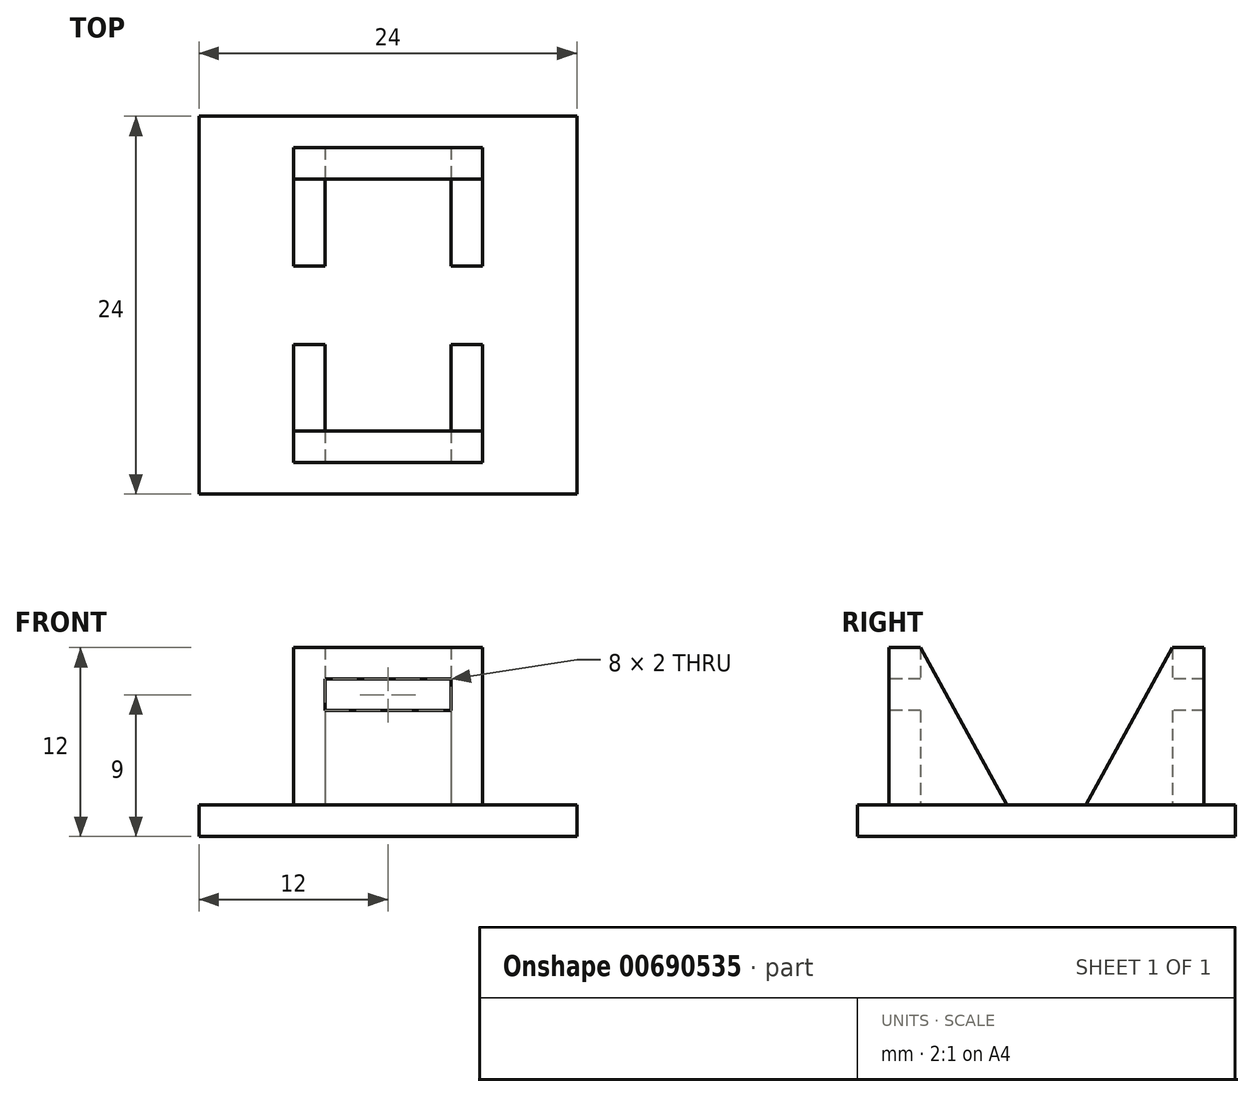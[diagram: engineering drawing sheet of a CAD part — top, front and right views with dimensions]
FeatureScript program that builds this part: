
annotation { "Feature Type Name" : "Feature", "Feature Type Description" : "" }
export const myFeature = defineFeature(function(context is Context, id is Id, definition is map)
    precondition{}
    {
        {
            var Q0;
            Q0=qCreatedBy(makeId("Top.planeOp"),FACE);
            var sketch = newSketch(context, id + "F0", { "sketchPlane" : qUnion([Q0])});
            skLineSegment(sketch, "E0.bottom", {"start": v(12, 12) * mm, "end": v(-12, 12) * mm});
            skLineSegment(sketch, "E0.top", {"start": v(12, -12) * mm, "end": v(-12, -12) * mm});
            skLineSegment(sketch, "E0.left", {"start": v(12, 12) * mm, "end": v(12, -12) * mm});
            skLineSegment(sketch, "E0.right", {"start": v(-12, 12) * mm, "end": v(-12, -12) * mm});
            skPoint(sketch, "E0.middle", {"position": v(0, 0) * mm});
            skLineSegment(sketch, "E1", {"start": v(0, 0) * mm, "end": v(-12, 0) * mm, "construction": true});
            skLineSegment(sketch, "E2", {"start": v(-6, 0) * mm, "end": v(-6, 2.5) * mm, "construction": true});
            skLineSegment(sketch, "E3", {"start": v(-6, 2.5) * mm, "end": v(-6, 10) * mm});
            skLineSegment(sketch, "E4", {"start": v(-6, 10) * mm, "end": v(0, 10) * mm});
            skLineSegment(sketch, "E5.0", {"start": v(-4, 8) * mm, "end": v(0, 8) * mm});
            skLineSegment(sketch, "E5.1", {"start": v(-4, 2.5) * mm, "end": v(-4, 8) * mm});
            skLineSegment(sketch, "E6", {"start": v(-6, 2.5) * mm, "end": v(-4, 2.5) * mm});
            skLineSegment(sketch, "E7.MirrorCS", {"start": v(6, 10) * mm, "end": v(0, 10) * mm});
            skLineSegment(sketch, "E8.MirrorCS", {"start": v(4, 8) * mm, "end": v(0, 8) * mm});
            skLineSegment(sketch, "E9.MirrorCS", {"start": v(4, 2.5) * mm, "end": v(4, 8) * mm});
            skLineSegment(sketch, "E10.MirrorCS", {"start": v(6, 2.5) * mm, "end": v(6, 10) * mm});
            skLineSegment(sketch, "E11.MirrorCS", {"start": v(6, 2.5) * mm, "end": v(4, 2.5) * mm});
            skLineSegment(sketch, "E12.MirrorCS", {"start": v(-6, -2.5) * mm, "end": v(-4, -2.5) * mm});
            skLineSegment(sketch, "E13.MirrorCS", {"start": v(6, -2.5) * mm, "end": v(4, -2.5) * mm});
            skLineSegment(sketch, "E14.MirrorCS", {"start": v(4, -2.5) * mm, "end": v(4, -8) * mm});
            skLineSegment(sketch, "E15.MirrorCS", {"start": v(6, -2.5) * mm, "end": v(6, -10) * mm});
            skLineSegment(sketch, "E16.MirrorCS", {"start": v(6, -10) * mm, "end": v(0, -10) * mm});
            skLineSegment(sketch, "E17.MirrorCS", {"start": v(4, -8) * mm, "end": v(0, -8) * mm});
            skLineSegment(sketch, "E18.MirrorCS", {"start": v(-4, -8) * mm, "end": v(0, -8) * mm});
            skLineSegment(sketch, "E19.MirrorCS", {"start": v(-6, -10) * mm, "end": v(0, -10) * mm});
            skLineSegment(sketch, "E20.MirrorCS", {"start": v(-6, -2.5) * mm, "end": v(-6, -10) * mm});
            skLineSegment(sketch, "E21.MirrorCS", {"start": v(-4, -2.5) * mm, "end": v(-4, -8) * mm});
            skSolve(sketch);
        }
        {
            var Q0;
            Q0=makeQuery(id+"F0.imprint","IMPRINT",FACE,{"disambiguationData":[TD([[makeQuery(id+"F0.imprint","IMPRINT",EDGE,{"derivedFrom":sQuery(id+"F0.wireOp",EDGE,"E0.bottom")}),1.0]])]});
            var Q1;
            Q1=makeQuery(id+"F0.imprint","IMPRINT",FACE,{"disambiguationData":[TD([[makeQuery(id+"F0.imprint","IMPRINT",EDGE,{"derivedFrom":sQuery(id+"F0.wireOp",EDGE,"E3")}),-1.0]])]});
            var Q2;
            Q2=makeQuery(id+"F0.imprint","IMPRINT",FACE,{"disambiguationData":[TD([[makeQuery(id+"F0.imprint","IMPRINT",EDGE,{"derivedFrom":sQuery(id+"F0.wireOp",EDGE,"E12.MirrorCS")}),-1.0]])]});
            extrude(context, id + "F1", {"entities" : qUnion([Q0, Q1, Q2]), "oppositeDirection" : true, "depth" : 2 * mm, "offsetDistance" : 25 * mm});
        }
        {
            var Q0;
            Q0=makeQuery(id+"F0.imprint","IMPRINT",FACE,{"disambiguationData":[TD([[makeQuery(id+"F0.imprint","IMPRINT",EDGE,{"derivedFrom":sQuery(id+"F0.wireOp",EDGE,"E3")}),-1.0]])]});
            var Q1;
            Q1=makeQuery(id+"F0.imprint","IMPRINT",FACE,{"disambiguationData":[TD([[makeQuery(id+"F0.imprint","IMPRINT",EDGE,{"derivedFrom":sQuery(id+"F0.wireOp",EDGE,"E12.MirrorCS")}),-1.0]])]});
            extrude(context, id + "F2", {"entities" : qUnion([Q0, Q1]), "operationType" : NewBodyOperationType.ADD, "depth" : 10 * mm, "offsetDistance" : 25 * mm});
        }
        {
            var Q0;
            Q0=makeQuery(id+"F2.opExtrude","CAP_EDGE",EDGE,{"disambiguationData":[OSD([sQuery(id+"F0.wireOp",EDGE,"E6")])],"isStart":false});
            var Q1;
            Q1=makeQuery(id+"F2.opExtrude","CAP_EDGE",EDGE,{"disambiguationData":[OSD([sQuery(id+"F0.wireOp",EDGE,"E11.MirrorCS")])],"isStart":false});
            chamfer(context, id + "F3", {"entities" : qUnion([Q0, Q1]), "chamferType" : ChamferType.TWO_OFFSETS, "width1" : 5.5 * mm, "oppositeDirection" : false, "width2" : 10 * mm, "tangentPropagation" : true});
        }
        {
            var Q0;
            Q0=makeQuery(id+"F2.opExtrude","CAP_EDGE",EDGE,{"disambiguationData":[OSD([sQuery(id+"F0.wireOp",EDGE,"E13.MirrorCS")])],"isStart":false});
            var Q1;
            Q1=makeQuery(id+"F2.opExtrude","CAP_EDGE",EDGE,{"disambiguationData":[OSD([sQuery(id+"F0.wireOp",EDGE,"E12.MirrorCS")])],"isStart":false});
            chamfer(context, id + "F4", {"entities" : qUnion([Q0, Q1]), "chamferType" : ChamferType.TWO_OFFSETS, "width1" : 5.5 * mm, "oppositeDirection" : false, "width2" : 10 * mm, "tangentPropagation" : true});
        }
        {
            var Q0;
            Q0=makeQuery(id+"F2.opExtrude","SWEPT_FACE",FACE,{"disambiguationData":[OSD([sQuery(id+"F0.wireOp",EDGE,"E16.MirrorCS"),sQuery(id+"F0.wireOp",EDGE,"E19.MirrorCS")])]});
            var sketch = newSketch(context, id + "F5", { "sketchPlane" : qUnion([Q0])});
            skLineSegment(sketch, "E22.bottom", {"start": v(-6, 10) * mm, "end": v(-4, 10) * mm});
            skLineSegment(sketch, "E22.top", {"start": v(-6, 8) * mm, "end": v(-4, 8) * mm});
            skLineSegment(sketch, "E22.left", {"start": v(-6, 10) * mm, "end": v(-6, 8) * mm});
            skLineSegment(sketch, "E22.right", {"start": v(-4, 10) * mm, "end": v(-4, 8) * mm});
            skLineSegment(sketch, "E23.bottom", {"start": v(6, 10) * mm, "end": v(4, 10) * mm});
            skLineSegment(sketch, "E23.top", {"start": v(6, 8) * mm, "end": v(4, 8) * mm});
            skLineSegment(sketch, "E23.left", {"start": v(6, 10) * mm, "end": v(6, 8) * mm});
            skLineSegment(sketch, "E23.right", {"start": v(4, 10) * mm, "end": v(4, 8) * mm});
            skLineSegment(sketch, "E24", {"start": v(-4, 8) * mm, "end": v(4, 8) * mm});
            skLineSegment(sketch, "E25", {"start": v(4, 8) * mm, "end": v(4, 6) * mm});
            skLineSegment(sketch, "E26", {"start": v(4, 6) * mm, "end": v(-4, 6) * mm});
            skLineSegment(sketch, "E27", {"start": v(-4, 6) * mm, "end": v(-4, 8) * mm});
            skSolve(sketch);
        }
        {
            var Q0;
            Q0=makeQuery(id+"F5.imprint","IMPRINT",FACE,{"disambiguationData":[TD([[makeQuery(id+"F5.imprint","IMPRINT",EDGE,{"derivedFrom":sQuery(id+"F5.wireOp",EDGE,"E24")}),-1.0]])]});
            extrude(context, id + "F6", {"entities" : qUnion([Q0]), "operationType" : NewBodyOperationType.REMOVE, "oppositeDirection" : true, "depth" : 25 * mm, "offsetDistance" : 25 * mm});
        }
    });
